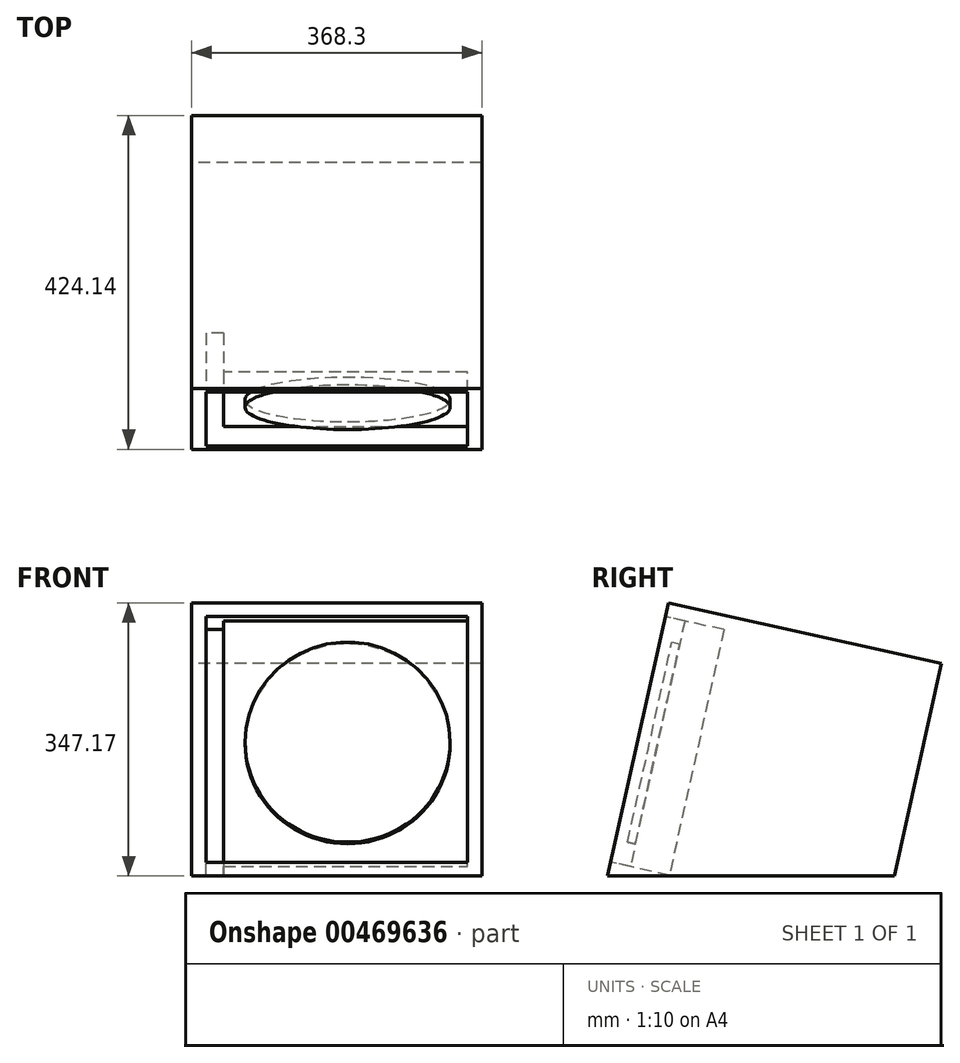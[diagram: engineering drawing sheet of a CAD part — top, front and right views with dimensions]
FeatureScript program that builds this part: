
annotation { "Feature Type Name" : "Feature", "Feature Type Description" : "" }
export const myFeature = defineFeature(function(context is Context, id is Id, definition is map)
    precondition{}
    {
        {
            var Q0;
            Q0=qCreatedBy(makeId("Right.planeOp"),FACE);
            var sketch = newSketch(context, id + "F0", { "sketchPlane" : qUnion([Q0])});
            skLineSegment(sketch, "E0", {"start": v(0, 0) * mm, "end": v(76.97, 347.17) * mm});
            skLineSegment(sketch, "E1", {"start": v(76.97, 347.17) * mm, "end": v(424.14, 270.2) * mm});
            skLineSegment(sketch, "E2", {"start": v(424.14, 270.2) * mm, "end": v(364.23, 0) * mm});
            skLineSegment(sketch, "E3", {"start": v(364.23, 0) * mm, "end": v(0, 0) * mm});
            skSolve(sketch);
        }
        {
            var Q0;
            Q0=makeQuery(id+"F0.imprint","IMPRINT",FACE,{"disambiguationData":[TD([[makeQuery(id+"F0.imprint","IMPRINT",EDGE,{"derivedFrom":sQuery(id+"F0.wireOp",EDGE,"E0")}),-1.0]])]});
            extrude(context, id + "F1", {"entities" : qUnion([Q0]), "depth" : 368.3 * mm});
        }
        {
            var Q0;
            Q0=makeQuery(id+"F1.opExtrude","SWEPT_FACE",FACE,{"disambiguationData":[OSD([sQuery(id+"F0.wireOp",EDGE,"E0")])]});
            var sketch = newSketch(context, id + "F2", { "sketchPlane" : qUnion([Q0])});
            skLineSegment(sketch, "E4", {"start": v(18.03, 337.57) * mm, "end": v(18.03, 18.03) * mm});
            skLineSegment(sketch, "E5", {"start": v(18.03, 18.03) * mm, "end": v(350.27, 18.03) * mm});
            skLineSegment(sketch, "E6", {"start": v(350.27, 18.03) * mm, "end": v(350.27, 337.57) * mm});
            skLineSegment(sketch, "E7", {"start": v(350.27, 337.57) * mm, "end": v(18.03, 337.57) * mm});
            skSolve(sketch);
        }
        {
            var Q0;
            Q0=makeQuery(id+"F2.imprint","IMPRINT",FACE,{"disambiguationData":[TD([[makeQuery(id+"F2.imprint","IMPRINT",EDGE,{"derivedFrom":sQuery(id+"F2.wireOp",EDGE,"E4")}),1.0]])]});
            extrude(context, id + "F3", {"entities" : qUnion([Q0]), "operationType" : NewBodyOperationType.REMOVE, "oppositeDirection" : true, "depth" : 25.4 * mm});
        }
        {
            var Q0;
            Q0=makeQuery(id+"F3.boolean.opBoolean","COPY",FACE,{"derivedFrom":makeQuery(id+"F3.opExtrude","CAP_FACE",FACE,{"disambiguationData":[OSD([sQuery(id+"F2.wireOp",EDGE,"E4"),sQuery(id+"F2.wireOp",EDGE,"E5"),sQuery(id+"F2.wireOp",EDGE,"E6"),sQuery(id+"F2.wireOp",EDGE,"E7")])],"isStart":false})});
            var sketch = newSketch(context, id + "F4", { "sketchPlane" : qUnion([Q0])});
            skCircle(sketch, "E8", {"center": v(197.87, 177.8) * mm, "radius": 130.18 * mm});
            skPoint(sketch, "E8.centerSnap0", {"position": v(197.87, 337.57) * mm});
            skPoint(sketch, "E9", {"position": v(350.27, 177.8) * mm});
            skSolve(sketch);
        }
        {
            var Q0;
            Q0=makeQuery(id+"F4.imprint","IMPRINT",FACE,{"disambiguationData":[TD([[makeQuery(id+"F4.imprint","IMPRINT",EDGE,{"derivedFrom":sQuery(id+"F4.wireOp",EDGE,"E8")}),1.0]])]});
            extrude(context, id + "F5", {"entities" : qUnion([Q0]), "operationType" : NewBodyOperationType.ADD, "depth" : 10.16 * mm});
        }
        {
            var Q0;
            Q0=makeQuery(id+"F3.boolean.opBoolean","COPY",FACE,{"derivedFrom":makeQuery(id+"F3.opExtrude","CAP_FACE",FACE,{"disambiguationData":[OSD([sQuery(id+"F2.wireOp",EDGE,"E4"),sQuery(id+"F2.wireOp",EDGE,"E5"),sQuery(id+"F2.wireOp",EDGE,"E6"),sQuery(id+"F2.wireOp",EDGE,"E7")])],"isStart":false})});
            var sketch = newSketch(context, id + "F6", { "sketchPlane" : qUnion([Q0])});
            skLineSegment(sketch, "E10.bottom", {"start": v(18.03, 337.57) * mm, "end": v(40.26, 337.57) * mm});
            skLineSegment(sketch, "E10.top", {"start": v(18.03, 18.03) * mm, "end": v(40.26, 18.03) * mm});
            skLineSegment(sketch, "E10.left", {"start": v(18.03, 337.57) * mm, "end": v(18.03, 18.03) * mm});
            skLineSegment(sketch, "E10.right", {"start": v(40.26, 337.57) * mm, "end": v(40.26, 18.03) * mm});
            skSolve(sketch);
        }
        {
            var Q0;
            Q0=makeQuery(id+"F6.imprint","IMPRINT",FACE,{"disambiguationData":[TD([[makeQuery(id+"F6.imprint","IMPRINT",EDGE,{"derivedFrom":sQuery(id+"F6.wireOp",EDGE,"E10.bottom")}),1.0]])]});
            extrude(context, id + "F7", {"entities" : qUnion([Q0]), "operationType" : NewBodyOperationType.REMOVE, "oppositeDirection" : true, "depth" : 50.8 * mm});
        }
    });
